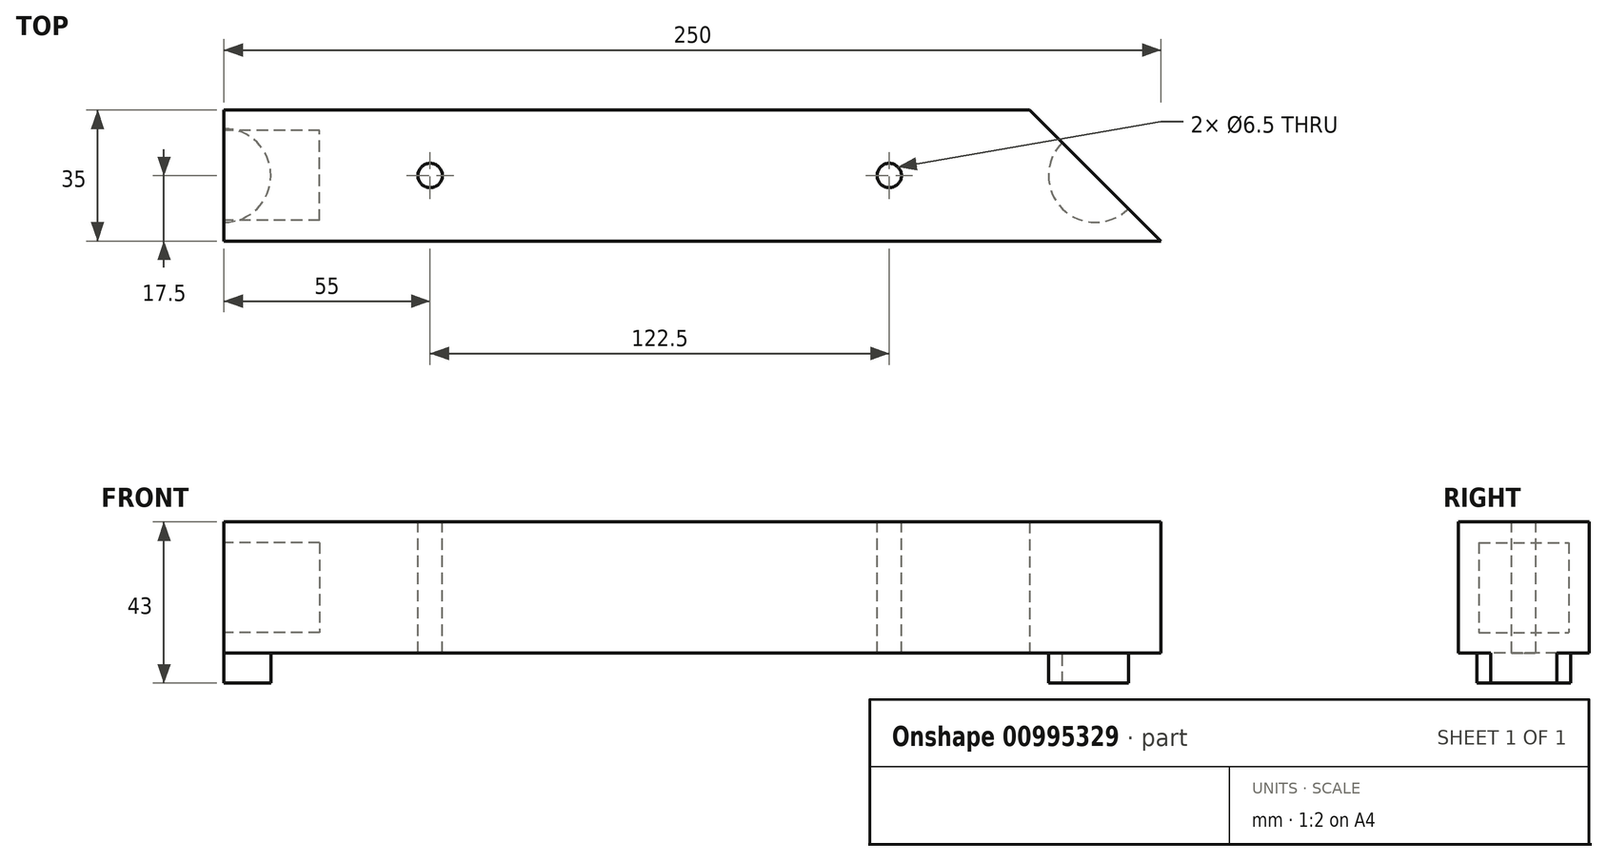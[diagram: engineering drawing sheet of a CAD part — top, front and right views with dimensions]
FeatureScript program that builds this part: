
annotation { "Feature Type Name" : "Feature", "Feature Type Description" : "" }
export const myFeature = defineFeature(function(context is Context, id is Id, definition is map)
    precondition{}
    {
        {
            var Q0;
            Q0=qCreatedBy(makeId("Top.planeOp"),FACE);
            var sketch = newSketch(context, id + "F0", { "sketchPlane" : qUnion([Q0])});
            skLineSegment(sketch, "E0.bottom", {"start": v(125, -17.5) * mm, "end": v(-125, -17.5) * mm});
            skLineSegment(sketch, "E0.top", {"start": v(90, 17.5) * mm, "end": v(-125, 17.5) * mm});
            skLineSegment(sketch, "E0.right", {"start": v(-125, -17.5) * mm, "end": v(-125, 17.5) * mm});
            skPoint(sketch, "E0.middle", {"position": v(0, 0) * mm});
            skPoint(sketch, "E1", {"position": v(90, 17.5) * mm});
            skLineSegment(sketch, "E2", {"start": v(125, -17.5) * mm, "end": v(90, 17.5) * mm});
            skPoint(sketch, "E0.left.end.orphan", {"position": v(125, 17.5) * mm});
            skSolve(sketch);
        }
        {
            var Q0;
            Q0=makeQuery(id+"F0.imprint","IMPRINT",FACE,{"disambiguationData":[TD([[makeQuery(id+"F0.imprint","IMPRINT",EDGE,{"derivedFrom":sQuery(id+"F0.wireOp",EDGE,"E0.bottom")}),-1.0]])]});
            extrude(context, id + "F1", {"entities" : qUnion([Q0]), "depth" : 35 * mm, "offsetDistance" : 25 * mm});
        }
        {
            var Q0;
            Q0=makeQuery(id+"F1.opExtrude","SWEPT_FACE",FACE,{"disambiguationData":[OSD([sQuery(id+"F0.wireOp",EDGE,"E0.right")])]});
            var sketch = newSketch(context, id + "F2", { "sketchPlane" : qUnion([Q0])});
            skLineSegment(sketch, "E3.0", {"start": v(-12, 29.5) * mm, "end": v(-12, 5.5) * mm});
            skLineSegment(sketch, "E3.1", {"start": v(12, 29.5) * mm, "end": v(-12, 29.5) * mm});
            skLineSegment(sketch, "E4.0", {"start": v(12, 5.5) * mm, "end": v(-12, 5.5) * mm});
            skLineSegment(sketch, "E4.1", {"start": v(12, 29.5) * mm, "end": v(12, 5.5) * mm});
            skSolve(sketch);
        }
        {
            var Q0;
            Q0=makeQuery(id+"F2.imprint","IMPRINT",FACE,{"disambiguationData":[TD([[makeQuery(id+"F2.imprint","IMPRINT",EDGE,{"derivedFrom":sQuery(id+"F2.wireOp",EDGE,"E3.0")}),1.0]])]});
            extrude(context, id + "F3", {"entities" : qUnion([Q0]), "operationType" : NewBodyOperationType.REMOVE, "oppositeDirection" : true, "depth" : 25.5 * mm, "offsetDistance" : 25 * mm});
        }
        {
            var Q0;
            Q0=makeQuery(id+"F1.opExtrude","CAP_FACE",FACE,{"disambiguationData":[OSD([sQuery(id+"F0.wireOp",EDGE,"E0.bottom"),sQuery(id+"F0.wireOp",EDGE,"E0.top"),sQuery(id+"F0.wireOp",EDGE,"E0.right"),sQuery(id+"F0.wireOp",EDGE,"E2")])],"isStart":false});
            var sketch = newSketch(context, id + "F4", { "sketchPlane" : qUnion([Q0])});
            skPoint(sketch, "E5", {"position": v(52.5, 0) * mm});
            skPoint(sketch, "E6", {"position": v(107.5, 0) * mm});
            skPoint(sketch, "E7", {"position": v(-125, 0) * mm});
            skPoint(sketch, "E8", {"position": v(-70, 0) * mm});
            skSolve(sketch);
        }
        {
            var Q0;
            Q0=sQuery(id+"F4.wireOp",VERTEX,"E5");
            var Q1;
            Q1=sQuery(id+"F4.wireOp",VERTEX,"E8");
            var Q2;
            Q2=makeQuery(id+"F1.opExtrude","SWEPT_BODY",BODY,{"disambiguationData":[OSD([sQuery(id+"F0.wireOp",EDGE,"E0.bottom"),sQuery(id+"F0.wireOp",EDGE,"E0.top"),sQuery(id+"F0.wireOp",EDGE,"E0.right"),sQuery(id+"F0.wireOp",EDGE,"E2")])]});
            hole(context, id + "F5", {"style" : HoleStyle.SIMPLE, "endStyle" : HoleEndStyle.BLIND, "holeDiameter" : 6.5 * mm, "majorDiameter" : 5 * mm, "holeDepth" : 35 * mm, "isTappedThrough" : true, "tappedDepth" : 12 * mm, "tapClearance" : 3, "locations" : qUnion([Q0, Q1]), "scope" : qUnion([Q2])});
        }
        {
            var Q0;
            Q0=makeQuery(id+"F1.opExtrude","CAP_FACE",FACE,{"disambiguationData":[OSD([sQuery(id+"F0.wireOp",EDGE,"E0.bottom"),sQuery(id+"F0.wireOp",EDGE,"E0.top"),sQuery(id+"F0.wireOp",EDGE,"E0.right"),sQuery(id+"F0.wireOp",EDGE,"E2")])],"isStart":true});
            var sketch = newSketch(context, id + "F6", { "sketchPlane" : qUnion([Q0])});
            skCircle(sketch, "E9", {"center": v(107.5, 0) * mm, "radius": 12.5 * mm});
            skSolve(sketch);
        }
        {
            var Q0;
            {var subQ0=sQuery(id+"F6.wireOp",EDGE,"E9");var subQ1=makeQuery(id+"F1.opExtrude","CAP_EDGE",EDGE,{"disambiguationData":[OSD([sQuery(id+"F0.wireOp",EDGE,"E2")])],"isStart":true});var subQ2=makeQuery(id+"F6.imprint","INTERSECT",VERTEX,{"disambiguationData":[OD(0.0)],"derivedFrom":[subQ1,subQ0]});Q0=makeQuery(id+"F6.imprint","IMPRINT",FACE,{"disambiguationData":[TD([[makeQuery(id+"F6.imprint","IMPRINT",EDGE,{"disambiguationData":[TD([[subQ2,-1.0]])],"derivedFrom":subQ0}),1.0]])]});}
            extrude(context, id + "F7", {"entities" : qUnion([Q0]), "operationType" : NewBodyOperationType.ADD, "depth" : 8 * mm, "offsetDistance" : 25 * mm});
        }
        {
            var Q0;
            Q0=makeQuery(id+"F1.opExtrude","CAP_FACE",FACE,{"disambiguationData":[OSD([sQuery(id+"F0.wireOp",EDGE,"E0.bottom"),sQuery(id+"F0.wireOp",EDGE,"E0.top"),sQuery(id+"F0.wireOp",EDGE,"E0.right"),sQuery(id+"F0.wireOp",EDGE,"E2")])],"isStart":true});
            var sketch = newSketch(context, id + "F8", { "sketchPlane" : qUnion([Q0])});
            skCircle(sketch, "E10", {"center": v(-125, 0) * mm, "radius": 12.5 * mm});
            skSolve(sketch);
        }
        {
            var Q0;
            {var subQ0=sQuery(id+"F8.wireOp",EDGE,"E10");var subQ1=makeQuery(id+"F1.opExtrude","CAP_EDGE",EDGE,{"disambiguationData":[OSD([sQuery(id+"F0.wireOp",EDGE,"E0.right")])],"isStart":true});var subQ2=makeQuery(id+"F8.imprint","INTERSECT",VERTEX,{"disambiguationData":[OD(0.0)],"derivedFrom":[subQ1,subQ0]});Q0=makeQuery(id+"F8.imprint","IMPRINT",FACE,{"disambiguationData":[TD([[makeQuery(id+"F8.imprint","IMPRINT",EDGE,{"disambiguationData":[TD([[subQ2,1.0]])],"derivedFrom":subQ0}),1.0]])]});}
            extrude(context, id + "F9", {"entities" : qUnion([Q0]), "operationType" : NewBodyOperationType.ADD, "depth" : 8 * mm, "offsetDistance" : 25 * mm});
        }
    });
